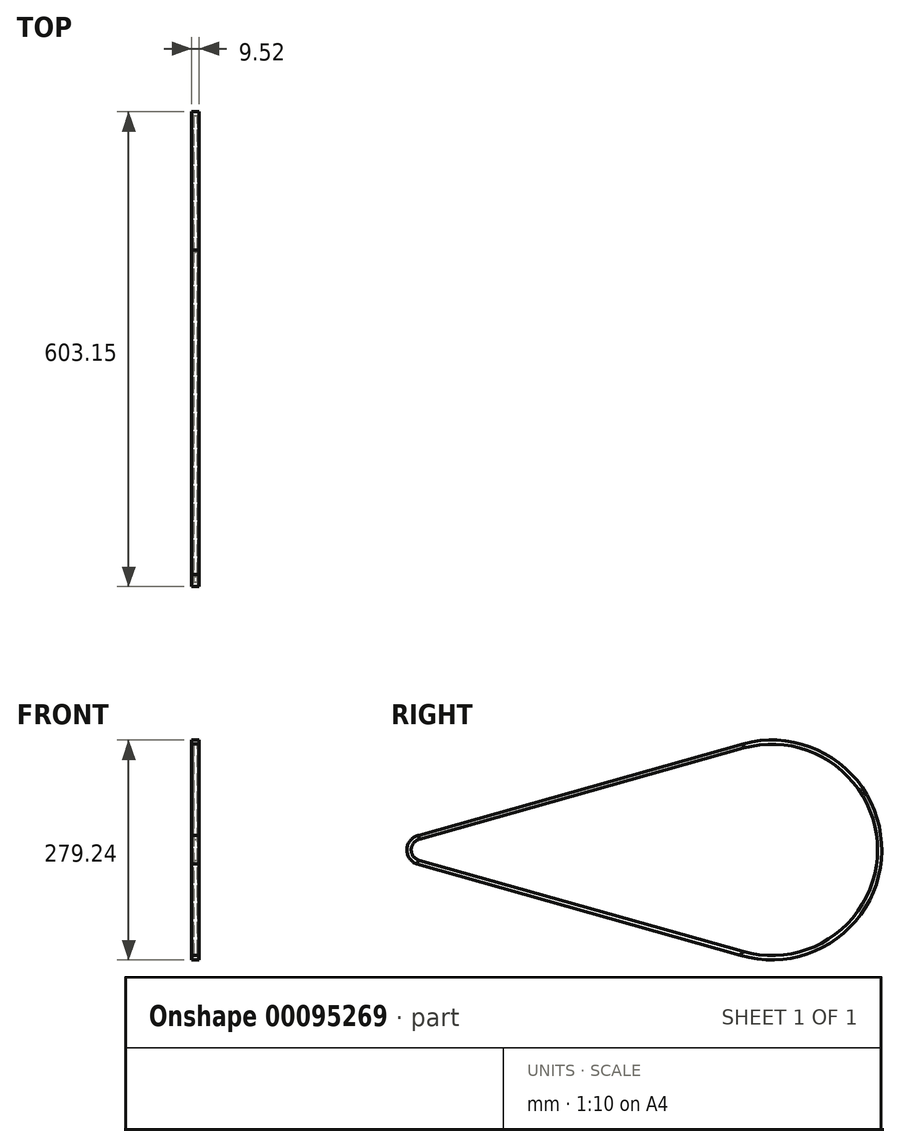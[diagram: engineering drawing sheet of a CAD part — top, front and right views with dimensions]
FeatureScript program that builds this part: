
annotation { "Feature Type Name" : "Feature", "Feature Type Description" : "" }
export const myFeature = defineFeature(function(context is Context, id is Id, definition is map)
    precondition{}
    {
        {
            var Q0;
            Q0=qCreatedBy(makeId("Right.planeOp"),FACE);
            var sketch = newSketch(context, id + "F0", { "sketchPlane" : qUnion([Q0])});
            skArc(sketch, "E0", {"start": v(411.75, -128.34) * mm, "mid": v(581.3, 0) * mm, "end": v(411.75, 128.34) * mm});
            skArc(sketch, "E1", {"start": v(0, 12.22) * mm, "mid": v(-9.25, 0) * mm, "end": v(0, -12.22) * mm});
            skLineSegment(sketch, "E2", {"start": v(411.75, 128.34) * mm, "end": v(0, 12.22) * mm});
            skLineSegment(sketch, "E3", {"start": v(0, -12.22) * mm, "end": v(411.75, -128.34) * mm});
            skPoint(sketch, "E4", {"position": v(0, 12.22) * mm});
            skSolve(sketch);
        }
        {
            var Q0;
            Q0=qCreatedBy(makeId("Front.planeOp"),FACE);
            var sketch = newSketch(context, id + "F1", { "sketchPlane" : qUnion([Q0])});
            skLineSegment(sketch, "E5", {"start": v(-2.47, 13.17) * mm, "end": v(2.47, 13.17) * mm});
            skLineSegment(sketch, "E6", {"start": v(2.47, 13.17) * mm, "end": v(4.76, 18.72) * mm});
            skLineSegment(sketch, "E7", {"start": v(4.76, 18.72) * mm, "end": v(-4.76, 18.72) * mm});
            skLineSegment(sketch, "E8", {"start": v(-4.76, 18.72) * mm, "end": v(-2.47, 13.17) * mm});
            skPoint(sketch, "E9", {"position": v(0, 13.17) * mm});
            skSolve(sketch);
        }
        {
            var Q0;
            Q0 = qSketchRegion(id + "F1", true);
            var Q1;
            Q1 = qConstructionFilter(qBodyType(qCreatedBy(id + "F0" ,EDGE), BodyType.WIRE), ConstructionObject.NO);
            sweep(context, id + "F2", {"profiles" : qUnion([Q0]), "path" : qUnion([Q1])});
        }
    });
